# Revit family: for update_26844CHN_new
name_source: partatom
category: Plumbing Fixtures
revit_build: Autodesk Revit 2018 (Build: 20170223_1515(x64)
units: mm (PartAtom-declared; Revit-internal decimal feet)

## family parameters
Always vertical = No
Cut with Voids When Loaded = No
OmniClass Number = 23.31.25.00
OmniClass Title = Toilet and Bath Specialties
Part Type = Normal
Room Calculation Point = No
Round Connector Dimension = Use Diameter
Shared = No
Work Plane-Based = Yes

## types (4) — shared parameters
Always visible = Yes
BIMobject category = Showers
Default Elevation = 1219.2 mm  [stored 4 ft]
Description = Rainfinity Shelf 500
Design country = Germany
EAN code = 4059625235706
Edition number = 1
IFC Classification = Furnishing Element
Manufacturer = Hansgrohe
Manufacturer country = Germany
Manufacturer name = hansgrohe
Material 2 = Hansgrohe - Plastic - Graphite
Model = 26844CHN
OmniClass Code = 23-31 25 00
OmniClass Description = Toilet and Bath Specialties
Product Guid = 3cd22548-4cc3-4d2f-9e14-6dd4cfd51659
Product SKU = 26844CHN
Product data url = https://bimobject.com
Product family = Rainfinity
Product group = Shelfs
Product name = 26844CHN Rainfinity Shelf 500
Product url = https://pro.hansgrohe.com
QR code = https://bimobject.com
UNSPSC Code = 301815
URL = https://www.hansgrohe.com
Weight Net (Kg) = 1

## per-type parameters (varying)
| type | Material 1 |
| 990 Polished Gold Optic | Hansgrohe - Metal - 997 Polished Gold Optic |
| 677 Matte Black | Hansgrohe - Metal - 677 Matte Black |
| 347 Brushed Black Chrome | Hansgrohe - Metal - 347 Brushed Black Chrome |
| 147 Brushed Bronze | Hansgrohe - Metal - 147 Brushed Bronze |

note: [stored X ft] marks values corroborated as IEEE doubles in the binary element streams (Revit-internal decimal feet)

## geometry (parser evidence)
native form markers: Sweep x2
no freeform markers — native parametric forms only
